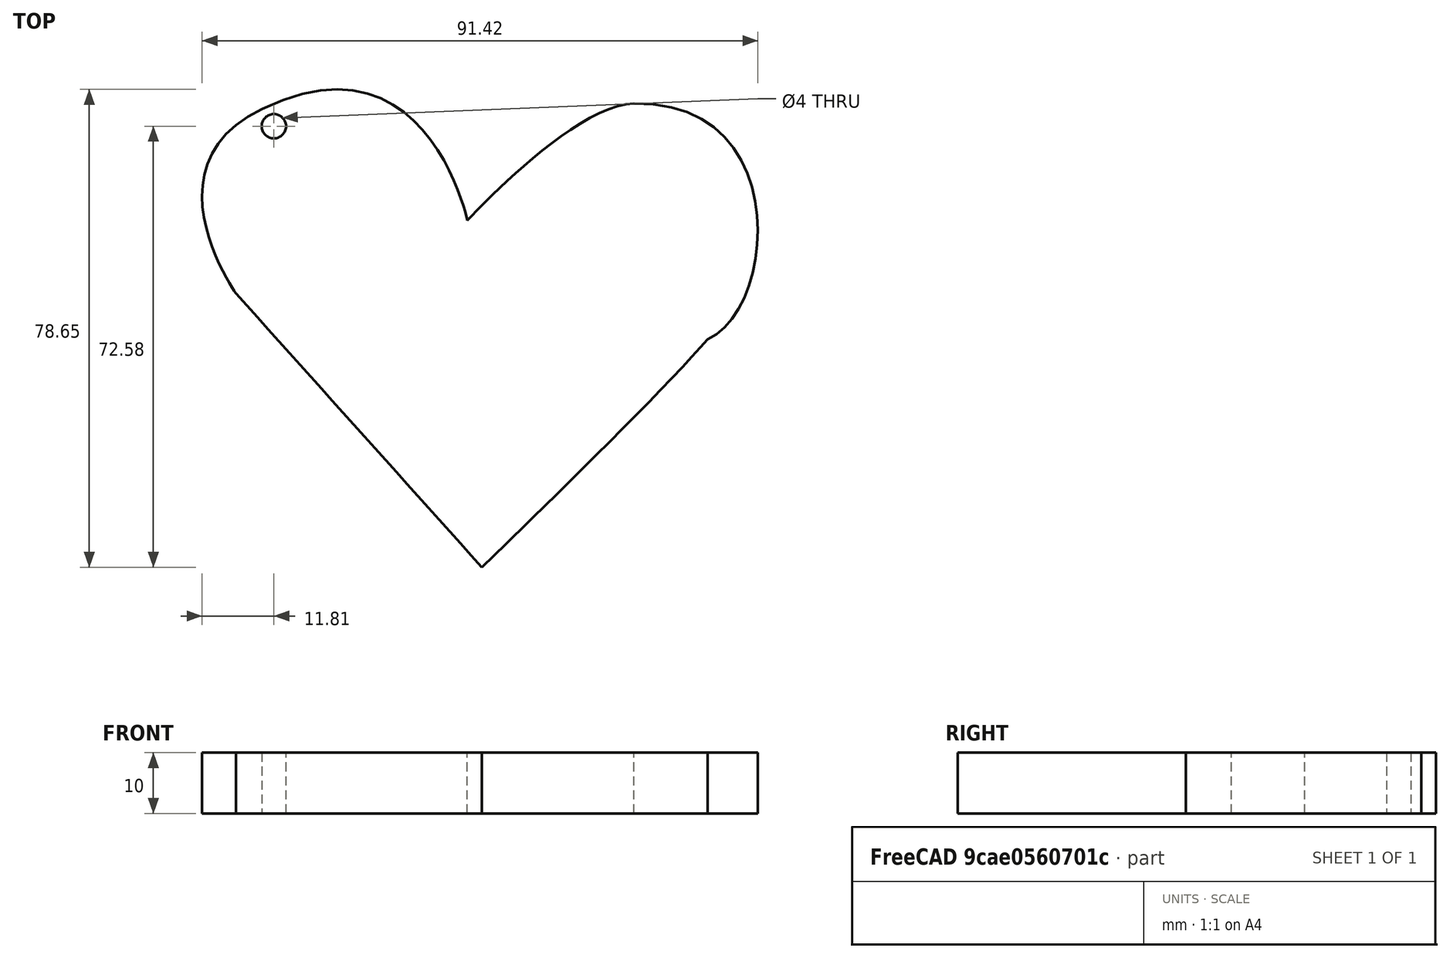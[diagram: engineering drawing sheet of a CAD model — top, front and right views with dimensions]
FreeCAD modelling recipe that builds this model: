
FCSTD DOCUMENT  (FreeCAD 0.20R29410 (Git))
Label: Corazon
License: Creative Commons Attribution-NonCommercial-ShareAlike
LicenseURL: http://creativecommons.org/licenses/by-nc-sa/4.0/
objects: Part::Feature×1, Part::Extrusion×1, Part::Cylinder×1, Part::Cut×1
note: 4 computed .brp shape members not serialized (recipe doc carries the construction recipe); baked Part::Feature solids carry a one-line shape summary decoded from their .brp

FEATURE [Part::Feature] path2246  label="Corazon"
  shape: bbox 98.76 x 83.24 x 2e-07 mm, 0 faces, 0 solids (baked)
FEATURE [Part::Extrusion] Extrude
  Base = -> path2246
  Dir = (0,0,3)
  DirMode = 0
  FaceMakerClass = Part::FaceMakerBullseye
  LengthFwd = 10
  LengthRev = 0
  Solid = true
  Symmetric = false
FEATURE [Part::Cylinder] Cylinder  label="Cilindro"
  Angle = 360
  AttacherType = Attacher::AttachEngine3D
  FirstAngle = 0
  Height = 12
  Placement = pos=(59.98,-74.8,0) rot=(0,0,1;0rad)
  Radius = 2
  SecondAngle = 0
FEATURE [Part::Cut] Cut
  Base = -> Extrude
  Tool = -> Cylinder
